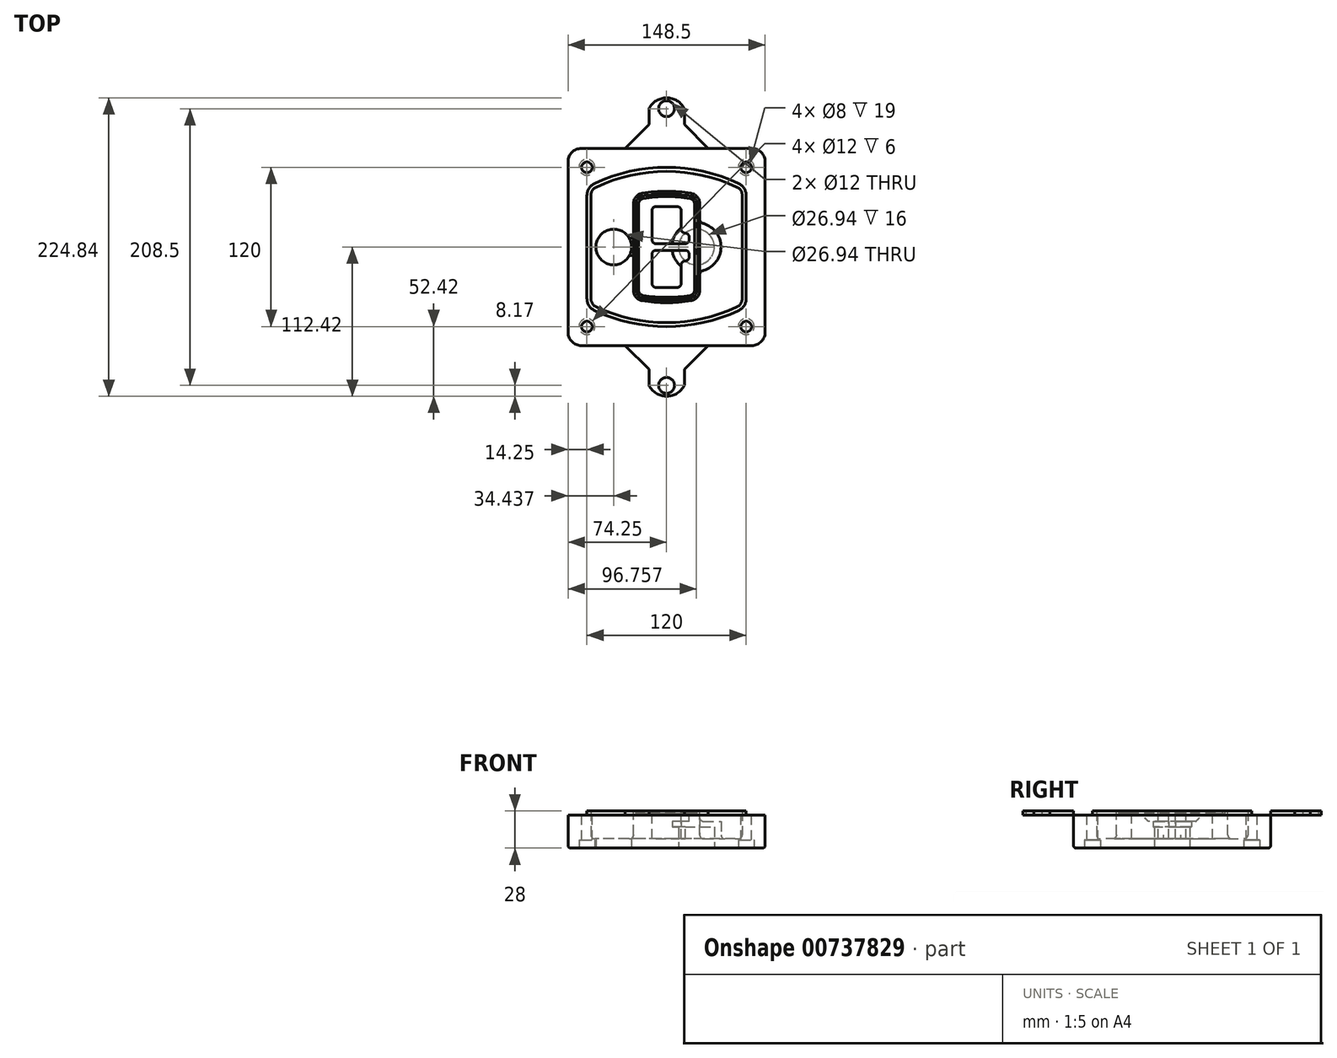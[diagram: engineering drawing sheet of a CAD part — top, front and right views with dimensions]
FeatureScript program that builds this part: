
annotation { "Feature Type Name" : "Feature", "Feature Type Description" : "" }
export const myFeature = defineFeature(function(context is Context, id is Id, definition is map)
    precondition{}
    {
        {
            var Q0;
            Q0=qCreatedBy(makeId("Top.planeOp"),FACE);
            var sketch = newSketch(context, id + "F0", { "sketchPlane" : qUnion([Q0])});
            skPoint(sketch, "E0.rect.middle", {"position": v(0, 0) * mm});
            skLineSegment(sketch, "E1.bottom", {"start": v(-64.25, -74.25) * mm, "end": v(64.25, -74.25) * mm});
            skLineSegment(sketch, "E1.top", {"start": v(-64.25, 74.25) * mm, "end": v(64.25, 74.25) * mm});
            skLineSegment(sketch, "E1.left", {"start": v(-74.25, -64.25) * mm, "end": v(-74.25, 64.25) * mm});
            skLineSegment(sketch, "E1.right", {"start": v(74.25, -64.25) * mm, "end": v(74.25, 64.25) * mm});
            skLineSegment(sketch, "E2", {"start": v(-74.25, 74.25) * mm, "end": v(74.25, -74.25) * mm, "construction": true});
            skLineSegment(sketch, "E3", {"start": v(74.25, 74.25) * mm, "end": v(-74.25, -74.25) * mm, "construction": true});
            skCircle(sketch, "E4", {"center": v(-60, 60) * mm, "radius": 4 * mm});
            skCircle(sketch, "E5", {"center": v(60, 60) * mm, "radius": 4 * mm});
            skCircle(sketch, "E6", {"center": v(60, -60) * mm, "radius": 4 * mm});
            skCircle(sketch, "E7", {"center": v(-60, -60) * mm, "radius": 4 * mm});
            skLineSegment(sketch, "E8", {"start": v(-60, 60) * mm, "end": v(60, 60) * mm, "construction": true});
            skLineSegment(sketch, "E9", {"start": v(60, 60) * mm, "end": v(60, -60) * mm, "construction": true});
            skLineSegment(sketch, "E10", {"start": v(60, -60) * mm, "end": v(-60, -60) * mm, "construction": true});
            skLineSegment(sketch, "E11", {"start": v(-60, -60) * mm, "end": v(-60, 60) * mm, "construction": true});
            skLineSegment(sketch, "E12", {"start": v(-60, 38.83) * mm, "end": v(-60, -38.83) * mm});
            skLineSegment(sketch, "E13", {"start": v(60, 38.83) * mm, "end": v(60, -38.83) * mm});
            skArc(sketch, "E14", {"start": v(54.26, 47.88) * mm, "mid": v(0, 60) * mm, "end": v(-54.26, 47.88) * mm});
            skArc(sketch, "E15", {"start": v(-54.26, -47.88) * mm, "mid": v(0, -60) * mm, "end": v(54.26, -47.88) * mm});
            skLineSegment(sketch, "E16", {"start": v(-60, 0) * mm, "end": v(60, 0) * mm, "construction": true});
            skPoint(sketch, "E17.visualSharp", {"position": v(-60, -45) * mm});
            skArc(sketch, "E17.filletArc", {"start": v(-60, -38.83) * mm, "mid": v(-58.44, -44.2) * mm, "end": v(-54.26, -47.88) * mm});
            skPoint(sketch, "E18.visualSharp", {"position": v(-60, 45) * mm});
            skArc(sketch, "E18.filletArc", {"start": v(-54.26, 47.88) * mm, "mid": v(-58.44, 44.2) * mm, "end": v(-60, 38.83) * mm});
            skPoint(sketch, "E19.visualSharp", {"position": v(60, 45) * mm});
            skArc(sketch, "E19.filletArc", {"start": v(60, 38.83) * mm, "mid": v(58.44, 44.2) * mm, "end": v(54.26, 47.88) * mm});
            skPoint(sketch, "E20.visualSharp", {"position": v(60, -45) * mm});
            skArc(sketch, "E20.filletArc", {"start": v(54.26, -47.88) * mm, "mid": v(58.44, -44.2) * mm, "end": v(60, -38.83) * mm});
            skPoint(sketch, "E21.visualSharp", {"position": v(-74.25, 74.25) * mm});
            skArc(sketch, "E21.filletArc", {"start": v(-64.25, 74.25) * mm, "mid": v(-71.32, 71.32) * mm, "end": v(-74.25, 64.25) * mm});
            skPoint(sketch, "E22.visualSharp", {"position": v(74.25, 74.25) * mm});
            skArc(sketch, "E22.filletArc", {"start": v(74.25, 64.25) * mm, "mid": v(71.32, 71.32) * mm, "end": v(64.25, 74.25) * mm});
            skPoint(sketch, "E23.visualSharp", {"position": v(74.25, -74.25) * mm});
            skArc(sketch, "E23.filletArc", {"start": v(64.25, -74.25) * mm, "mid": v(71.32, -71.32) * mm, "end": v(74.25, -64.25) * mm});
            skPoint(sketch, "E24.visualSharp", {"position": v(-74.25, -74.25) * mm});
            skArc(sketch, "E24.filletArc", {"start": v(-74.25, -64.25) * mm, "mid": v(-71.32, -71.32) * mm, "end": v(-64.25, -74.25) * mm});
            skArc(sketch, "E25.0", {"start": v(57, 38.83) * mm, "mid": v(55.9, 42.58) * mm, "end": v(52.98, 45.17) * mm});
            skLineSegment(sketch, "E25.1", {"start": v(57, 38.83) * mm, "end": v(57, -38.83) * mm});
            skArc(sketch, "E25.2", {"start": v(52.98, -45.17) * mm, "mid": v(55.9, -42.58) * mm, "end": v(57, -38.83) * mm});
            skArc(sketch, "E25.3", {"start": v(-52.98, -45.17) * mm, "mid": v(0, -57) * mm, "end": v(52.98, -45.17) * mm});
            skArc(sketch, "E25.4", {"start": v(-57, -38.83) * mm, "mid": v(-55.9, -42.58) * mm, "end": v(-52.98, -45.17) * mm});
            skArc(sketch, "E25.5", {"start": v(52.98, 45.17) * mm, "mid": v(0, 57) * mm, "end": v(-52.98, 45.17) * mm});
            skLineSegment(sketch, "E25.6", {"start": v(-57, 38.83) * mm, "end": v(-57, -38.83) * mm});
            skArc(sketch, "E25.7", {"start": v(-52.98, 45.17) * mm, "mid": v(-55.9, 42.58) * mm, "end": v(-57, 38.83) * mm});
            skArc(sketch, "E26.0", {"start": v(-55.96, 51.5) * mm, "mid": v(-61.82, 46.33) * mm, "end": v(-64, 38.83) * mm});
            skArc(sketch, "E26.1", {"start": v(55.96, 51.5) * mm, "mid": v(0, 64) * mm, "end": v(-55.96, 51.5) * mm});
            skArc(sketch, "E26.2", {"start": v(64, 38.83) * mm, "mid": v(61.82, 46.33) * mm, "end": v(55.96, 51.5) * mm});
            skLineSegment(sketch, "E26.3", {"start": v(64, 38.83) * mm, "end": v(64, -38.83) * mm});
            skArc(sketch, "E26.4", {"start": v(55.96, -51.5) * mm, "mid": v(61.82, -46.33) * mm, "end": v(64, -38.83) * mm});
            skLineSegment(sketch, "E26.5", {"start": v(-64, 38.83) * mm, "end": v(-64, -38.83) * mm});
            skArc(sketch, "E26.6", {"start": v(-55.96, -51.5) * mm, "mid": v(0, -64) * mm, "end": v(55.96, -51.5) * mm});
            skArc(sketch, "E26.7", {"start": v(-64, -38.83) * mm, "mid": v(-61.82, -46.33) * mm, "end": v(-55.96, -51.5) * mm});
            skSolve(sketch);
        }
        {
            var Q0;
            Q0=makeQuery(id+"F0.imprint","IMPRINT",FACE,{"disambiguationData":[TD([[makeQuery(id+"F0.imprint","IMPRINT",EDGE,{"derivedFrom":sQuery(id+"F0.wireOp",EDGE,"E1.bottom")}),1.0]])]});
            var Q1;
            Q1=makeQuery(id+"F0.imprint","IMPRINT",FACE,{"disambiguationData":[TD([[makeQuery(id+"F0.imprint","IMPRINT",EDGE,{"derivedFrom":sQuery(id+"F0.wireOp",EDGE,"E12")}),1.0]])]});
            var Q2;
            Q2=makeQuery(id+"F0.imprint","IMPRINT",FACE,{"disambiguationData":[TD([[makeQuery(id+"F0.imprint","IMPRINT",EDGE,{"derivedFrom":sQuery(id+"F0.wireOp",EDGE,"E25.0")}),1.0]])]});
            var Q3;
            Q3=makeQuery(id+"F0.imprint","IMPRINT",FACE,{"disambiguationData":[TD([[makeQuery(id+"F0.imprint","IMPRINT",EDGE,{"derivedFrom":sQuery(id+"F0.wireOp",EDGE,"E12")}),-1.0]])]});
            extrude(context, id + "F1", {"entities" : qUnion([Q0, Q1, Q2, Q3]), "oppositeDirection" : true, "depth" : 25 * mm});
        }
        {
            var Q0;
            Q0=makeQuery(id+"F0.imprint","IMPRINT",FACE,{"disambiguationData":[TD([[makeQuery(id+"F0.imprint","IMPRINT",EDGE,{"derivedFrom":sQuery(id+"F0.wireOp",EDGE,"E12")}),1.0]])]});
            extrude(context, id + "F2", {"entities" : qUnion([Q0]), "operationType" : NewBodyOperationType.ADD, "depth" : 3 * mm});
        }
        {
            var Q0;
            Q0=makeQuery(id+"F0.imprint","IMPRINT",FACE,{"disambiguationData":[TD([[makeQuery(id+"F0.imprint","IMPRINT",EDGE,{"derivedFrom":sQuery(id+"F0.wireOp",EDGE,"E25.0")}),1.0]])]});
            extrude(context, id + "F3", {"entities" : qUnion([Q0]), "operationType" : NewBodyOperationType.REMOVE, "oppositeDirection" : true, "depth" : 18 * mm});
        }
        {
            var Q0;
            Q0=makeQuery(id+"F2.opExtrude","CAP_FACE",FACE,{"disambiguationData":[OSD([sQuery(id+"F0.wireOp",EDGE,"E12"),sQuery(id+"F0.wireOp",EDGE,"E13"),sQuery(id+"F0.wireOp",EDGE,"E14"),sQuery(id+"F0.wireOp",EDGE,"E15"),sQuery(id+"F0.wireOp",EDGE,"E17.filletArc"),sQuery(id+"F0.wireOp",EDGE,"E18.filletArc"),sQuery(id+"F0.wireOp",EDGE,"E19.filletArc"),sQuery(id+"F0.wireOp",EDGE,"E20.filletArc"),sQuery(id+"F0.wireOp",EDGE,"E25.0"),sQuery(id+"F0.wireOp",EDGE,"E25.1"),sQuery(id+"F0.wireOp",EDGE,"E25.2"),sQuery(id+"F0.wireOp",EDGE,"E25.3"),sQuery(id+"F0.wireOp",EDGE,"E25.4"),sQuery(id+"F0.wireOp",EDGE,"E25.5"),sQuery(id+"F0.wireOp",EDGE,"E25.6"),sQuery(id+"F0.wireOp",EDGE,"E25.7")])],"isStart":false});
            var sketch = newSketch(context, id + "F4", { "sketchPlane" : qUnion([Q0])});
            skArc(sketch, "E27.0", {"start": v(-18.34, -40.45) * mm, "mid": v(0, -42) * mm, "end": v(18.34, -40.45) * mm});
            skArc(sketch, "E28.0", {"start": v(18.34, 40.45) * mm, "mid": v(0, 42) * mm, "end": v(-18.34, 40.45) * mm});
            skLineSegment(sketch, "E29", {"start": v(-25, 32.57) * mm, "end": v(-25, -32.57) * mm});
            skLineSegment(sketch, "E30", {"start": v(25, 32.57) * mm, "end": v(25, -32.57) * mm});
            skLineSegment(sketch, "E31", {"start": v(-25, 39.1) * mm, "end": v(25, 39.1) * mm, "construction": true});
            skLineSegment(sketch, "E32", {"start": v(-25, -39.1) * mm, "end": v(25, -39.1) * mm, "construction": true});
            skPoint(sketch, "E33.visualSharp", {"position": v(-25, 39.1) * mm});
            skArc(sketch, "E33.filletArc", {"start": v(-18.34, 40.45) * mm, "mid": v(-23.11, 37.73) * mm, "end": v(-25, 32.57) * mm});
            skPoint(sketch, "E34.visualSharp", {"position": v(25, 39.1) * mm});
            skArc(sketch, "E34.filletArc", {"start": v(25, 32.57) * mm, "mid": v(23.11, 37.73) * mm, "end": v(18.34, 40.45) * mm});
            skPoint(sketch, "E35.visualSharp", {"position": v(25, -39.1) * mm});
            skArc(sketch, "E35.filletArc", {"start": v(18.34, -40.45) * mm, "mid": v(23.11, -37.73) * mm, "end": v(25, -32.57) * mm});
            skPoint(sketch, "E36.visualSharp", {"position": v(-25, -39.1) * mm});
            skArc(sketch, "E36.filletArc", {"start": v(-25, -32.57) * mm, "mid": v(-23.11, -37.73) * mm, "end": v(-18.34, -40.45) * mm});
            skArc(sketch, "E37.0", {"start": v(52.98, 45.17) * mm, "mid": v(0, 57) * mm, "end": v(-52.98, 45.17) * mm});
            skArc(sketch, "E37.1", {"start": v(-52.98, 45.17) * mm, "mid": v(-55.9, 42.58) * mm, "end": v(-57, 38.83) * mm});
            skLineSegment(sketch, "E37.2", {"start": v(-57, 38.83) * mm, "end": v(-57, -38.83) * mm});
            skArc(sketch, "E37.3", {"start": v(-57, -38.83) * mm, "mid": v(-55.9, -42.58) * mm, "end": v(-52.98, -45.17) * mm});
            skArc(sketch, "E37.4", {"start": v(-52.98, -45.17) * mm, "mid": v(0, -57) * mm, "end": v(52.98, -45.17) * mm});
            skArc(sketch, "E37.5", {"start": v(52.98, -45.17) * mm, "mid": v(55.9, -42.58) * mm, "end": v(57, -38.83) * mm});
            skLineSegment(sketch, "E37.6", {"start": v(57, 38.83) * mm, "end": v(57, -38.83) * mm});
            skArc(sketch, "E37.7", {"start": v(57, 38.83) * mm, "mid": v(55.9, 42.58) * mm, "end": v(52.98, 45.17) * mm});
            skLineSegment(sketch, "E38.0", {"start": v(23, 32.57) * mm, "end": v(23, -32.57) * mm});
            skArc(sketch, "E38.1", {"start": v(18, -38.48) * mm, "mid": v(21.58, -36.44) * mm, "end": v(23, -32.57) * mm});
            skArc(sketch, "E38.2", {"start": v(-18, -38.48) * mm, "mid": v(0, -40) * mm, "end": v(18, -38.48) * mm});
            skArc(sketch, "E38.3", {"start": v(-23, -32.57) * mm, "mid": v(-21.58, -36.44) * mm, "end": v(-18, -38.48) * mm});
            skLineSegment(sketch, "E38.4", {"start": v(-23, 32.57) * mm, "end": v(-23, -32.57) * mm});
            skArc(sketch, "E38.5", {"start": v(23, 32.57) * mm, "mid": v(21.58, 36.44) * mm, "end": v(18, 38.48) * mm});
            skArc(sketch, "E38.6", {"start": v(-18, 38.48) * mm, "mid": v(-21.58, 36.44) * mm, "end": v(-23, 32.57) * mm});
            skArc(sketch, "E38.7", {"start": v(18, 38.48) * mm, "mid": v(0, 40) * mm, "end": v(-18, 38.48) * mm});
            skArc(sketch, "E39.0", {"start": v(21, 32.57) * mm, "mid": v(20.06, 35.15) * mm, "end": v(17.67, 36.5) * mm});
            skLineSegment(sketch, "E39.1", {"start": v(21, 32.57) * mm, "end": v(21, -32.57) * mm});
            skArc(sketch, "E39.2", {"start": v(17.67, -36.5) * mm, "mid": v(20.06, -35.15) * mm, "end": v(21, -32.57) * mm});
            skArc(sketch, "E39.3", {"start": v(-17.67, -36.5) * mm, "mid": v(0, -38) * mm, "end": v(17.67, -36.5) * mm});
            skArc(sketch, "E39.4", {"start": v(-21, -32.57) * mm, "mid": v(-20.06, -35.15) * mm, "end": v(-17.67, -36.5) * mm});
            skArc(sketch, "E39.5", {"start": v(17.67, 36.5) * mm, "mid": v(0, 38) * mm, "end": v(-17.67, 36.5) * mm});
            skLineSegment(sketch, "E39.6", {"start": v(-21, 32.57) * mm, "end": v(-21, -32.57) * mm});
            skArc(sketch, "E39.7", {"start": v(-17.67, 36.5) * mm, "mid": v(-20.06, 35.15) * mm, "end": v(-21, 32.57) * mm});
            skLineSegment(sketch, "E40", {"start": v(-25, 0) * mm, "end": v(25, 0) * mm, "construction": true});
            skLineSegment(sketch, "E41", {"start": v(-11, 5.5) * mm, "end": v(-11, 27.5) * mm});
            skLineSegment(sketch, "E42", {"start": v(-8, 30.5) * mm, "end": v(8, 30.5) * mm});
            skLineSegment(sketch, "E43", {"start": v(11, 27.5) * mm, "end": v(11, 13.5) * mm});
            skLineSegment(sketch, "E44", {"start": v(14, 10.5) * mm, "end": v(14, 10.5) * mm});
            skLineSegment(sketch, "E45", {"start": v(17, 7.5) * mm, "end": v(17, 5.5) * mm});
            skLineSegment(sketch, "E46", {"start": v(14, 2.5) * mm, "end": v(-8, 2.5) * mm});
            skPoint(sketch, "E47.visualSharp", {"position": v(-11, 30.5) * mm});
            skArc(sketch, "E47.filletArc", {"start": v(-8, 30.5) * mm, "mid": v(-10.12, 29.62) * mm, "end": v(-11, 27.5) * mm});
            skPoint(sketch, "E48.visualSharp", {"position": v(11, 30.5) * mm});
            skArc(sketch, "E48.filletArc", {"start": v(11, 27.5) * mm, "mid": v(10.12, 29.62) * mm, "end": v(8, 30.5) * mm});
            skPoint(sketch, "E49.visualSharp", {"position": v(11, 10.5) * mm});
            skArc(sketch, "E49.filletArc", {"start": v(11, 13.5) * mm, "mid": v(11.88, 11.38) * mm, "end": v(14, 10.5) * mm});
            skPoint(sketch, "E50.visualSharp", {"position": v(17, 10.5) * mm});
            skArc(sketch, "E50.filletArc", {"start": v(17, 7.5) * mm, "mid": v(16.12, 9.62) * mm, "end": v(14, 10.5) * mm});
            skPoint(sketch, "E51.visualSharp", {"position": v(17, 2.5) * mm});
            skArc(sketch, "E51.filletArc", {"start": v(14, 2.5) * mm, "mid": v(16.12, 3.38) * mm, "end": v(17, 5.5) * mm});
            skPoint(sketch, "E52.visualSharp", {"position": v(-11, 2.5) * mm});
            skArc(sketch, "E52.filletArc", {"start": v(-11, 5.5) * mm, "mid": v(-10.12, 3.38) * mm, "end": v(-8, 2.5) * mm});
            skLineSegment(sketch, "E53.0.MirrorCS", {"start": v(14, -2.5) * mm, "end": v(-8, -2.5) * mm});
            skArc(sketch, "E54.0.MirrorCS", {"start": v(-11, -5.5) * mm, "mid": v(-10.12, -3.38) * mm, "end": v(-8, -2.5) * mm});
            skLineSegment(sketch, "E55.0.MirrorCS", {"start": v(-11, -5.5) * mm, "end": v(-11, -27.5) * mm});
            skArc(sketch, "E56.0.MirrorCS", {"start": v(-8, -30.5) * mm, "mid": v(-10.12, -29.62) * mm, "end": v(-11, -27.5) * mm});
            skLineSegment(sketch, "E57.0.MirrorCS", {"start": v(-8, -30.5) * mm, "end": v(8, -30.5) * mm});
            skArc(sketch, "E58.0.MirrorCS", {"start": v(11, -27.5) * mm, "mid": v(10.12, -29.62) * mm, "end": v(8, -30.5) * mm});
            skLineSegment(sketch, "E59.0.MirrorCS", {"start": v(11, -27.5) * mm, "end": v(11, -13.5) * mm});
            skArc(sketch, "E60.0.MirrorCS", {"start": v(11, -13.5) * mm, "mid": v(11.88, -11.38) * mm, "end": v(14, -10.5) * mm});
            skArc(sketch, "E61.0.MirrorCS", {"start": v(17, -7.5) * mm, "mid": v(16.12, -9.62) * mm, "end": v(14, -10.5) * mm});
            skLineSegment(sketch, "E62.0.MirrorCS", {"start": v(17, -7.5) * mm, "end": v(17, -5.5) * mm});
            skArc(sketch, "E63.0.MirrorCS", {"start": v(14, -2.5) * mm, "mid": v(16.12, -3.38) * mm, "end": v(17, -5.5) * mm});
            skSolve(sketch);
        }
        {
            var Q0;
            Q0=makeQuery(id+"F4.imprint","IMPRINT",FACE,{"disambiguationData":[TD([[makeQuery(id+"F4.imprint","IMPRINT",EDGE,{"derivedFrom":sQuery(id+"F4.wireOp",EDGE,"E27.0")}),1.0]])]});
            var Q1;
            Q1=makeQuery(id+"F4.imprint","IMPRINT",FACE,{"disambiguationData":[TD([[makeQuery(id+"F4.imprint","IMPRINT",EDGE,{"derivedFrom":sQuery(id+"F4.wireOp",EDGE,"E38.0")}),-1.0]])]});
            var Q2;
            Q2=makeQuery(id+"F4.imprint","IMPRINT",FACE,{"disambiguationData":[TD([[makeQuery(id+"F4.imprint","IMPRINT",EDGE,{"derivedFrom":sQuery(id+"F4.wireOp",EDGE,"E39.0")}),1.0]])]});
            extrude(context, id + "F5", {"entities" : qUnion([Q0, Q1, Q2]), "operationType" : NewBodyOperationType.ADD, "endBound" : BoundingType.UP_TO_NEXT, "oppositeDirection" : true, "depth" : 25 * mm});
        }
        {
            var Q0;
            Q0=makeQuery(id+"F4.imprint","IMPRINT",FACE,{"disambiguationData":[TD([[makeQuery(id+"F4.imprint","IMPRINT",EDGE,{"derivedFrom":sQuery(id+"F4.wireOp",EDGE,"E38.0")}),-1.0]])]});
            extrude(context, id + "F6", {"entities" : qUnion([Q0]), "operationType" : NewBodyOperationType.REMOVE, "oppositeDirection" : true, "depth" : 2 * mm});
        }
        {
            var Q0;
            Q0=makeQuery(id+"F1.opExtrude","CAP_FACE",FACE,{"disambiguationData":[OSD([sQuery(id+"F0.wireOp",EDGE,"E1.bottom"),sQuery(id+"F0.wireOp",EDGE,"E1.top"),sQuery(id+"F0.wireOp",EDGE,"E1.left"),sQuery(id+"F0.wireOp",EDGE,"E1.right"),sQuery(id+"F0.wireOp",EDGE,"E4"),sQuery(id+"F0.wireOp",EDGE,"E5"),sQuery(id+"F0.wireOp",EDGE,"E6"),sQuery(id+"F0.wireOp",EDGE,"E7"),sQuery(id+"F0.wireOp",EDGE,"E21.filletArc"),sQuery(id+"F0.wireOp",EDGE,"E22.filletArc"),sQuery(id+"F0.wireOp",EDGE,"E23.filletArc"),sQuery(id+"F0.wireOp",EDGE,"E24.filletArc")])],"isStart":false});
            var sketch = newSketch(context, id + "F7", { "sketchPlane" : qUnion([Q0])});
            skCircle(sketch, "E64", {"center": v(22.5, 0) * mm, "radius": 13.47 * mm});
            skCircle(sketch, "E65", {"center": v(-39.81, 0) * mm, "radius": 13.47 * mm});
            skLineSegment(sketch, "E66", {"start": v(74.25, 0) * mm, "end": v(-74.25, 0) * mm});
            skCircle(sketch, "E67", {"center": v(22.5, 0) * mm, "radius": 18.47 * mm});
            skCircle(sketch, "E68", {"center": v(60, -60) * mm, "radius": 6 * mm});
            skCircle(sketch, "E69", {"center": v(-60, -60) * mm, "radius": 6 * mm});
            skCircle(sketch, "E70", {"center": v(-60, 60) * mm, "radius": 6 * mm});
            skCircle(sketch, "E71", {"center": v(60, 60) * mm, "radius": 6 * mm});
            skSolve(sketch);
        }
        {
            var Q0;
            {var subQ1=sQuery(id+"F7.wireOp",EDGE,"E66");var subQ4=sQuery(id+"F7.wireOp",EDGE,"E64");var subQ6=makeQuery(id+"F7.imprint","INTERSECT",VERTEX,{"disambiguationData":[OD(0.0)],"derivedFrom":[subQ4,subQ1]});Q0=makeQuery(id+"F7.imprint","IMPRINT",FACE,{"disambiguationData":[TD([[makeQuery(id+"F7.imprint","IMPRINT",EDGE,{"disambiguationData":[TD([[subQ6,-1.0]])],"derivedFrom":subQ4}),-1.0]])]});}
            var Q1;
            {var subQ0=sQuery(id+"F7.wireOp",EDGE,"E66");var subQ1=sQuery(id+"F7.wireOp",EDGE,"E64");var subQ3=makeQuery(id+"F7.imprint","INTERSECT",VERTEX,{"disambiguationData":[OD(0.0)],"derivedFrom":[subQ1,subQ0]});Q1=makeQuery(id+"F7.imprint","IMPRINT",FACE,{"disambiguationData":[TD([[makeQuery(id+"F7.imprint","IMPRINT",EDGE,{"disambiguationData":[TD([[subQ3,-1.0]])],"derivedFrom":subQ1}),1.0]])]});}
            var Q2;
            {var subQ0=sQuery(id+"F7.wireOp",EDGE,"E66");var subQ1=sQuery(id+"F7.wireOp",EDGE,"E64");var subQ3=makeQuery(id+"F7.imprint","INTERSECT",VERTEX,{"disambiguationData":[OD(0.0)],"derivedFrom":[subQ1,subQ0]});Q2=makeQuery(id+"F7.imprint","IMPRINT",FACE,{"disambiguationData":[TD([[makeQuery(id+"F7.imprint","IMPRINT",EDGE,{"disambiguationData":[TD([[subQ3,1.0]])],"derivedFrom":subQ1}),1.0]])]});}
            var Q3;
            {var subQ1=sQuery(id+"F7.wireOp",EDGE,"E66");var subQ4=sQuery(id+"F7.wireOp",EDGE,"E64");var subQ6=makeQuery(id+"F7.imprint","INTERSECT",VERTEX,{"disambiguationData":[OD(0.0)],"derivedFrom":[subQ4,subQ1]});Q3=makeQuery(id+"F7.imprint","IMPRINT",FACE,{"disambiguationData":[TD([[makeQuery(id+"F7.imprint","IMPRINT",EDGE,{"disambiguationData":[TD([[subQ6,1.0]])],"derivedFrom":subQ4}),-1.0]])]});}
            extrude(context, id + "F8", {"entities" : qUnion([Q0, Q1, Q2, Q3]), "operationType" : NewBodyOperationType.ADD, "oppositeDirection" : true, "depth" : 20 * mm});
        }
        {
            var Q0;
            {var subQ0=sQuery(id+"F7.wireOp",EDGE,"E66");var subQ1=sQuery(id+"F7.wireOp",EDGE,"E64");var subQ3=makeQuery(id+"F7.imprint","INTERSECT",VERTEX,{"disambiguationData":[OD(0.0)],"derivedFrom":[subQ1,subQ0]});Q0=makeQuery(id+"F7.imprint","IMPRINT",FACE,{"disambiguationData":[TD([[makeQuery(id+"F7.imprint","IMPRINT",EDGE,{"disambiguationData":[TD([[subQ3,-1.0]])],"derivedFrom":subQ1}),1.0]])]});}
            var Q1;
            {var subQ0=sQuery(id+"F7.wireOp",EDGE,"E66");var subQ1=sQuery(id+"F7.wireOp",EDGE,"E64");var subQ3=makeQuery(id+"F7.imprint","INTERSECT",VERTEX,{"disambiguationData":[OD(0.0)],"derivedFrom":[subQ1,subQ0]});Q1=makeQuery(id+"F7.imprint","IMPRINT",FACE,{"disambiguationData":[TD([[makeQuery(id+"F7.imprint","IMPRINT",EDGE,{"disambiguationData":[TD([[subQ3,1.0]])],"derivedFrom":subQ1}),1.0]])]});}
            extrude(context, id + "F9", {"entities" : qUnion([Q0, Q1]), "operationType" : NewBodyOperationType.REMOVE, "oppositeDirection" : true, "depth" : 16 * mm});
        }
        {
            var Q0;
            {var subQ0=sQuery(id+"F7.wireOp",EDGE,"E66");var subQ1=sQuery(id+"F7.wireOp",EDGE,"E65");var subQ3=makeQuery(id+"F7.imprint","INTERSECT",VERTEX,{"disambiguationData":[OD(0.0)],"derivedFrom":[subQ1,subQ0]});Q0=makeQuery(id+"F7.imprint","IMPRINT",FACE,{"disambiguationData":[TD([[makeQuery(id+"F7.imprint","IMPRINT",EDGE,{"disambiguationData":[TD([[subQ3,-1.0]])],"derivedFrom":subQ1}),1.0]])]});}
            var Q1;
            {var subQ0=sQuery(id+"F7.wireOp",EDGE,"E66");var subQ1=sQuery(id+"F7.wireOp",EDGE,"E65");var subQ3=makeQuery(id+"F7.imprint","INTERSECT",VERTEX,{"disambiguationData":[OD(0.0)],"derivedFrom":[subQ1,subQ0]});Q1=makeQuery(id+"F7.imprint","IMPRINT",FACE,{"disambiguationData":[TD([[makeQuery(id+"F7.imprint","IMPRINT",EDGE,{"disambiguationData":[TD([[subQ3,1.0]])],"derivedFrom":subQ1}),1.0]])]});}
            extrude(context, id + "F10", {"entities" : qUnion([Q0, Q1]), "operationType" : NewBodyOperationType.REMOVE, "oppositeDirection" : true, "depth" : 25 * mm});
        }
        {
            var Q0;
            Q0=makeQuery(id+"F7.imprint","IMPRINT",FACE,{"disambiguationData":[TD([[makeQuery(id+"F7.imprint","IMPRINT",EDGE,{"derivedFrom":sQuery(id+"F7.wireOp",EDGE,"E68")}),1.0]])]});
            var Q1;
            Q1=makeQuery(id+"F7.imprint","IMPRINT",FACE,{"disambiguationData":[TD([[makeQuery(id+"F7.imprint","IMPRINT",EDGE,{"derivedFrom":makeQuery(id+"F1.opExtrude","CAP_EDGE",EDGE,{"disambiguationData":[OSD([sQuery(id+"F0.wireOp",EDGE,"E5")])],"isStart":false})}),-1.0]])]});
            var Q2;
            Q2=makeQuery(id+"F7.imprint","IMPRINT",FACE,{"disambiguationData":[TD([[makeQuery(id+"F7.imprint","IMPRINT",EDGE,{"derivedFrom":sQuery(id+"F7.wireOp",EDGE,"E69")}),1.0]])]});
            var Q3;
            Q3=makeQuery(id+"F7.imprint","IMPRINT",FACE,{"disambiguationData":[TD([[makeQuery(id+"F7.imprint","IMPRINT",EDGE,{"derivedFrom":makeQuery(id+"F1.opExtrude","CAP_EDGE",EDGE,{"disambiguationData":[OSD([sQuery(id+"F0.wireOp",EDGE,"E4")])],"isStart":false})}),-1.0]])]});
            var Q4;
            Q4=makeQuery(id+"F7.imprint","IMPRINT",FACE,{"disambiguationData":[TD([[makeQuery(id+"F7.imprint","IMPRINT",EDGE,{"derivedFrom":sQuery(id+"F7.wireOp",EDGE,"E70")}),1.0]])]});
            var Q5;
            Q5=makeQuery(id+"F7.imprint","IMPRINT",FACE,{"disambiguationData":[TD([[makeQuery(id+"F7.imprint","IMPRINT",EDGE,{"derivedFrom":makeQuery(id+"F1.opExtrude","CAP_EDGE",EDGE,{"disambiguationData":[OSD([sQuery(id+"F0.wireOp",EDGE,"E7")])],"isStart":false})}),-1.0]])]});
            var Q6;
            Q6=makeQuery(id+"F7.imprint","IMPRINT",FACE,{"disambiguationData":[TD([[makeQuery(id+"F7.imprint","IMPRINT",EDGE,{"derivedFrom":sQuery(id+"F7.wireOp",EDGE,"E71")}),1.0]])]});
            var Q7;
            Q7=makeQuery(id+"F7.imprint","IMPRINT",FACE,{"disambiguationData":[TD([[makeQuery(id+"F7.imprint","IMPRINT",EDGE,{"derivedFrom":makeQuery(id+"F1.opExtrude","CAP_EDGE",EDGE,{"disambiguationData":[OSD([sQuery(id+"F0.wireOp",EDGE,"E6")])],"isStart":false})}),-1.0]])]});
            extrude(context, id + "F11", {"entities" : qUnion([Q0, Q1, Q2, Q3, Q4, Q5, Q6, Q7]), "operationType" : NewBodyOperationType.REMOVE, "oppositeDirection" : true, "depth" : 6 * mm});
        }
        {
            var Q0;
            Q0=makeQuery(id+"F9.boolean.opBoolean","COPY",FACE,{"derivedFrom":makeQuery(id+"F9.opExtrude","CAP_FACE",FACE,{"disambiguationData":[OSD([sQuery(id+"F7.wireOp",EDGE,"E64")])],"isStart":false})});
            var sketch = newSketch(context, id + "F12", { "sketchPlane" : qUnion([Q0])});
            skArc(sketch, "E72.0", {"start": v(11, 14.45) * mm, "mid": v(6.45, 9.13) * mm, "end": v(4.2, 2.5) * mm});
            skArc(sketch, "E72.1", {"start": v(4.2, -2.5) * mm, "mid": v(6.45, -9.13) * mm, "end": v(11, -14.45) * mm});
            skLineSegment(sketch, "E73", {"start": v(4.2, -2.5) * mm, "end": v(14, -2.5) * mm});
            skLineSegment(sketch, "E74.0", {"start": v(14, 2.5) * mm, "end": v(4.2, 2.5) * mm});
            skArc(sketch, "E74.1", {"start": v(14, 2.5) * mm, "mid": v(16.12, 3.38) * mm, "end": v(17, 5.5) * mm});
            skLineSegment(sketch, "E74.2", {"start": v(17, 7.5) * mm, "end": v(17, 5.5) * mm});
            skArc(sketch, "E74.3", {"start": v(17, 7.5) * mm, "mid": v(16.12, 9.62) * mm, "end": v(14, 10.5) * mm});
            skArc(sketch, "E74.4", {"start": v(11, 13.5) * mm, "mid": v(11.88, 11.38) * mm, "end": v(14, 10.5) * mm});
            skLineSegment(sketch, "E74.5", {"start": v(11, 14.45) * mm, "end": v(11, 13.5) * mm});
            skLineSegment(sketch, "E74.7", {"start": v(14, -2.5) * mm, "end": v(4.2, -2.5) * mm});
            skArc(sketch, "E74.8", {"start": v(14, -2.5) * mm, "mid": v(16.12, -3.38) * mm, "end": v(17, -5.5) * mm});
            skLineSegment(sketch, "E74.9", {"start": v(17, -7.5) * mm, "end": v(17, -5.5) * mm});
            skArc(sketch, "E74.10", {"start": v(17, -7.5) * mm, "mid": v(16.12, -9.62) * mm, "end": v(14, -10.5) * mm});
            skArc(sketch, "E74.11", {"start": v(11, -13.5) * mm, "mid": v(11.88, -11.38) * mm, "end": v(14, -10.5) * mm});
            skLineSegment(sketch, "E74.12", {"start": v(11, -14.45) * mm, "end": v(11, -13.5) * mm});
            skPoint(sketch, "E75.orphan", {"position": v(11, -27.5) * mm});
            skPoint(sketch, "E76.orphan", {"position": v(-8, -2.5) * mm});
            skPoint(sketch, "E77.orphan", {"position": v(-8, 2.5) * mm});
            skPoint(sketch, "E78.orphan", {"position": v(11, 27.5) * mm});
            skSolve(sketch);
        }
        {
            var Q0;
            {var subQ7=sQuery(id+"F12.wireOp",EDGE,"E72.0");var subQ14=sQuery(id+"F12.wireOp",EDGE,"E72.1");var subQ16=sQuery(id+"F12.wireOp",EDGE,"E74.1");var subQ18=sQuery(id+"F12.wireOp",EDGE,"E74.8");Q0=qUnion([makeQuery(id+"F12.imprint","IMPRINT",FACE,{"disambiguationData":[TD([[makeQuery(id+"F12.imprint","IMPRINT",EDGE,{"derivedFrom":subQ7}),1.0]])]}),makeQuery(id+"F12.imprint","IMPRINT",FACE,{"disambiguationData":[TD([[makeQuery(id+"F12.imprint","IMPRINT",EDGE,{"derivedFrom":subQ14}),1.0]])]}),makeQuery(id+"F12.imprint","IMPRINT",FACE,{"disambiguationData":[TD([[makeQuery(id+"F12.imprint","IMPRINT",EDGE,{"derivedFrom":subQ16}),1.0]])]}),makeQuery(id+"F12.imprint","IMPRINT",FACE,{"disambiguationData":[TD([[makeQuery(id+"F12.imprint","IMPRINT",EDGE,{"derivedFrom":subQ18}),-1.0]])]})]);}
            var Q1;
            Q1=makeQuery(id+"F5.boolean.opBoolean","SPLIT",FACE,{"disambiguationData":[TD([makeQuery(id+"F5.opExtrude","SWEPT_FACE",FACE,{"disambiguationData":[OSD([sQuery(id+"F4.wireOp",EDGE,"E41")])]})])],"derivedFrom":makeQuery(id+"F3.boolean.opBoolean","COPY",FACE,{"derivedFrom":makeQuery(id+"F3.opExtrude","CAP_FACE",FACE,{"disambiguationData":[OSD([sQuery(id+"F0.wireOp",EDGE,"E25.0"),sQuery(id+"F0.wireOp",EDGE,"E25.1"),sQuery(id+"F0.wireOp",EDGE,"E25.2"),sQuery(id+"F0.wireOp",EDGE,"E25.3"),sQuery(id+"F0.wireOp",EDGE,"E25.4"),sQuery(id+"F0.wireOp",EDGE,"E25.5"),sQuery(id+"F0.wireOp",EDGE,"E25.6"),sQuery(id+"F0.wireOp",EDGE,"E25.7")])],"isStart":false})})});
            extrude(context, id + "F13", {"entities" : qUnion([Q0]), "operationType" : NewBodyOperationType.REMOVE, "endBound" : BoundingType.UP_TO_SURFACE, "endBoundEntityFace" : qUnion([Q1]), "depth" : 25 * mm});
        }
        {
            var Q0;
            Q0=makeQuery(id+"F3.boolean.opBoolean","COPY",EDGE,{"derivedFrom":makeQuery(id+"F3.opExtrude","CAP_EDGE",EDGE,{"disambiguationData":[OSD([sQuery(id+"F0.wireOp",EDGE,"E25.6")])],"isStart":false})});
            var Q1;
            Q1=makeQuery(id+"F8.boolean.opBoolean","INTERSECT",EDGE,{"derivedFrom":[makeQuery(id+"F5.opExtrude","SWEPT_FACE",FACE,{"disambiguationData":[OSD([sQuery(id+"F4.wireOp",EDGE,"E30")])]}),makeQuery(id+"F8.opExtrude","CAP_FACE",FACE,{"disambiguationData":[OSD([sQuery(id+"F7.wireOp",EDGE,"E67")])],"isStart":false})]});
            var Q2;
            Q2=makeQuery(id+"F8.boolean.opBoolean","INTERSECT",EDGE,{"disambiguationData":[OD(1.0)],"derivedFrom":[makeQuery(id+"F5.opExtrude","SWEPT_FACE",FACE,{"disambiguationData":[OSD([sQuery(id+"F4.wireOp",EDGE,"E30")])]}),makeQuery(id+"F8.opExtrude","SWEPT_FACE",FACE,{"disambiguationData":[OSD([sQuery(id+"F7.wireOp",EDGE,"E67")])]})]});
            var Q3;
            {var subQ0=sQuery(id+"F4.wireOp",EDGE,"E30");Q3=makeQuery(id+"F8.boolean.opBoolean","SPLIT",EDGE,{"disambiguationData":[TD([makeQuery(id+"F5.opExtrude","SWEPT_FACE",FACE,{"disambiguationData":[OSD([sQuery(id+"F4.wireOp",EDGE,"E35.filletArc")])]})])],"derivedFrom":makeQuery(id+"F5.opExtrude","CAP_EDGE",EDGE,{"disambiguationData":[OSD([subQ0])],"isStart":false})});}
            var Q4;
            {var subQ0=sQuery(id+"F0.wireOp",EDGE,"E25.7");var subQ1=sQuery(id+"F0.wireOp",EDGE,"E25.1");var subQ2=sQuery(id+"F0.wireOp",EDGE,"E25.6");var subQ3=sQuery(id+"F0.wireOp",EDGE,"E25.5");var subQ4=sQuery(id+"F0.wireOp",EDGE,"E25.4");var subQ5=sQuery(id+"F0.wireOp",EDGE,"E25.0");var subQ6=sQuery(id+"F0.wireOp",EDGE,"E25.2");var subQ7=sQuery(id+"F0.wireOp",EDGE,"E25.3");Q4=makeQuery(id+"F8.boolean.opBoolean","INTERSECT",EDGE,{"derivedFrom":[makeQuery(id+"F5.boolean.opBoolean","SPLIT",FACE,{"disambiguationData":[TD([makeQuery(id+"F2.opExtrude","SWEPT_FACE",FACE,{"disambiguationData":[OSD([subQ5])]})])],"derivedFrom":makeQuery(id+"F3.boolean.opBoolean","COPY",FACE,{"derivedFrom":makeQuery(id+"F3.opExtrude","CAP_FACE",FACE,{"disambiguationData":[OSD([subQ5,subQ1,subQ6,subQ7,subQ4,subQ3,subQ2,subQ0])],"isStart":false})})}),makeQuery(id+"F8.opExtrude","SWEPT_FACE",FACE,{"disambiguationData":[OSD([sQuery(id+"F7.wireOp",EDGE,"E67")])]})]});}
            var Q5;
            Q5=makeQuery(id+"F8.boolean.opBoolean","INTERSECT",EDGE,{"disambiguationData":[OD(0.0)],"derivedFrom":[makeQuery(id+"F5.opExtrude","SWEPT_FACE",FACE,{"disambiguationData":[OSD([sQuery(id+"F4.wireOp",EDGE,"E30")])]}),makeQuery(id+"F8.opExtrude","SWEPT_FACE",FACE,{"disambiguationData":[OSD([sQuery(id+"F7.wireOp",EDGE,"E67")])]})]});
            fillet(context, id + "F14", {"entities" : qUnion([Q0, Q1, Q2, Q3, Q4, Q5]), "radius" : 3 * mm, "tangentPropagation" : true, "allowEdgeOverflow" : false});
        }
        {
            var Q0;
            Q0=makeQuery(id+"F1.opExtrude","CAP_EDGE",EDGE,{"disambiguationData":[OSD([sQuery(id+"F0.wireOp",EDGE,"E1.bottom")])],"isStart":false});
            fillet(context, id + "F15", {"entities" : qUnion([Q0]), "radius" : 2 * mm, "tangentPropagation" : true, "allowEdgeOverflow" : false});
        }
        {
            var Q0;
            {var subQ0=sQuery(id+"F0.wireOp",EDGE,"E21.filletArc");var subQ1=sQuery(id+"F0.wireOp",EDGE,"E7");var subQ2=sQuery(id+"F0.wireOp",EDGE,"E6");var subQ3=sQuery(id+"F0.wireOp",EDGE,"E5");var subQ4=sQuery(id+"F0.wireOp",EDGE,"E4");var subQ5=sQuery(id+"F0.wireOp",EDGE,"E22.filletArc");var subQ6=sQuery(id+"F0.wireOp",EDGE,"E1.bottom");var subQ7=sQuery(id+"F0.wireOp",EDGE,"E1.right");var subQ8=sQuery(id+"F0.wireOp",EDGE,"E1.top");var subQ9=sQuery(id+"F0.wireOp",EDGE,"E1.left");var subQ10=sQuery(id+"F0.wireOp",EDGE,"E23.filletArc");var subQ11=sQuery(id+"F0.wireOp",EDGE,"E24.filletArc");Q0=makeQuery(id+"F2.boolean.opBoolean","SPLIT",FACE,{"disambiguationData":[TD([makeQuery(id+"F1.opExtrude","SWEPT_FACE",FACE,{"disambiguationData":[OSD([subQ6])]})])],"derivedFrom":makeQuery(id+"F1.opExtrude","CAP_FACE",FACE,{"disambiguationData":[OSD([subQ6,subQ8,subQ9,subQ7,subQ4,subQ3,subQ2,subQ1,subQ0,subQ5,subQ10,subQ11])],"isStart":true})});}
            var sketch = newSketch(context, id + "F16", { "sketchPlane" : qUnion([Q0])});
            skLineSegment(sketch, "E79", {"start": v(0, 74.25) * mm, "end": v(0, 104.25) * mm, "construction": true});
            skCircle(sketch, "E80", {"center": v(0, 104.25) * mm, "radius": 6 * mm});
            skLineSegment(sketch, "E81", {"start": v(-13.28, 92.25) * mm, "end": v(-13.28, 104.25) * mm});
            skArc(sketch, "E82", {"start": v(13.43, 104.25) * mm, "mid": v(0.08, 112.42) * mm, "end": v(-13.28, 104.25) * mm});
            skLineSegment(sketch, "E83", {"start": v(13.43, 104.25) * mm, "end": v(13.43, 92.25) * mm});
            skLineSegment(sketch, "E84", {"start": v(13.43, 92.25) * mm, "end": v(31.43, 74.25) * mm});
            skLineSegment(sketch, "E85", {"start": v(-13.28, 92.25) * mm, "end": v(-31.28, 74.25) * mm});
            skLineSegment(sketch, "E86", {"start": v(0, 0) * mm, "end": v(-74.25, 0) * mm});
            skLineSegment(sketch, "E87", {"start": v(-74.25, 0) * mm, "end": v(74.25, 0) * mm, "construction": true});
            skLineSegment(sketch, "E88.MirrorCS", {"start": v(-13.28, -92.25) * mm, "end": v(-31.28, -74.25) * mm});
            skLineSegment(sketch, "E89.MirrorCS", {"start": v(13.43, -92.25) * mm, "end": v(31.43, -74.25) * mm});
            skLineSegment(sketch, "E90.MirrorCS", {"start": v(13.43, -104.25) * mm, "end": v(13.43, -92.25) * mm});
            skArc(sketch, "E91.MirrorCS", {"start": v(13.43, -104.25) * mm, "mid": v(0.08, -112.42) * mm, "end": v(-13.28, -104.25) * mm});
            skLineSegment(sketch, "E92.MirrorCS", {"start": v(-13.28, -92.25) * mm, "end": v(-13.28, -104.25) * mm});
            skCircle(sketch, "E93.MirrorC", {"center": v(0, -104.25) * mm, "radius": 6 * mm});
            skLineSegment(sketch, "E94.MirrorCS", {"start": v(0, -74.25) * mm, "end": v(0, -104.25) * mm, "construction": true});
            skSolve(sketch);
        }
        {
            var Q0;
            Q0=makeQuery(id+"F16.imprint","IMPRINT",FACE,{"disambiguationData":[TD([[makeQuery(id+"F16.imprint","IMPRINT",EDGE,{"derivedFrom":sQuery(id+"F16.wireOp",EDGE,"E80")}),-1.0]])]});
            var Q1;
            Q1=makeQuery(id+"F2.opExtrude","CAP_FACE",FACE,{"disambiguationData":[OSD([sQuery(id+"F0.wireOp",EDGE,"E12"),sQuery(id+"F0.wireOp",EDGE,"E13"),sQuery(id+"F0.wireOp",EDGE,"E14"),sQuery(id+"F0.wireOp",EDGE,"E15"),sQuery(id+"F0.wireOp",EDGE,"E17.filletArc"),sQuery(id+"F0.wireOp",EDGE,"E18.filletArc"),sQuery(id+"F0.wireOp",EDGE,"E19.filletArc"),sQuery(id+"F0.wireOp",EDGE,"E20.filletArc"),sQuery(id+"F0.wireOp",EDGE,"E25.0"),sQuery(id+"F0.wireOp",EDGE,"E25.1"),sQuery(id+"F0.wireOp",EDGE,"E25.2"),sQuery(id+"F0.wireOp",EDGE,"E25.3"),sQuery(id+"F0.wireOp",EDGE,"E25.4"),sQuery(id+"F0.wireOp",EDGE,"E25.5"),sQuery(id+"F0.wireOp",EDGE,"E25.6"),sQuery(id+"F0.wireOp",EDGE,"E25.7")])],"isStart":false});
            extrude(context, id + "F17", {"entities" : qUnion([Q0]), "endBound" : BoundingType.UP_TO_SURFACE, "depth" : 25 * mm, "endBoundEntityFace" : qUnion([Q1]), "offsetDistance" : 25 * mm});
        }
        {
            var Q0;
            {var subQ0=sQuery(id+"F16.wireOp",EDGE,"E88.MirrorCS");Q0=makeQuery(id+"F16.imprint","IMPRINT",FACE,{"disambiguationData":[TD([[makeQuery(id+"F16.imprint","IMPRINT",EDGE,{"derivedFrom":subQ0}),-1.0]])]});}
            var Q1;
            Q1=makeQuery(id+"F2.opExtrude","CAP_FACE",FACE,{"disambiguationData":[OSD([sQuery(id+"F0.wireOp",EDGE,"E12"),sQuery(id+"F0.wireOp",EDGE,"E13"),sQuery(id+"F0.wireOp",EDGE,"E14"),sQuery(id+"F0.wireOp",EDGE,"E15"),sQuery(id+"F0.wireOp",EDGE,"E17.filletArc"),sQuery(id+"F0.wireOp",EDGE,"E18.filletArc"),sQuery(id+"F0.wireOp",EDGE,"E19.filletArc"),sQuery(id+"F0.wireOp",EDGE,"E20.filletArc"),sQuery(id+"F0.wireOp",EDGE,"E25.0"),sQuery(id+"F0.wireOp",EDGE,"E25.1"),sQuery(id+"F0.wireOp",EDGE,"E25.2"),sQuery(id+"F0.wireOp",EDGE,"E25.3"),sQuery(id+"F0.wireOp",EDGE,"E25.4"),sQuery(id+"F0.wireOp",EDGE,"E25.5"),sQuery(id+"F0.wireOp",EDGE,"E25.6"),sQuery(id+"F0.wireOp",EDGE,"E25.7")])],"isStart":false});
            extrude(context, id + "F18", {"entities" : qUnion([Q0]), "endBound" : BoundingType.UP_TO_SURFACE, "depth" : 25 * mm, "endBoundEntityFace" : qUnion([Q1]), "offsetDistance" : 25 * mm});
        }
    });
